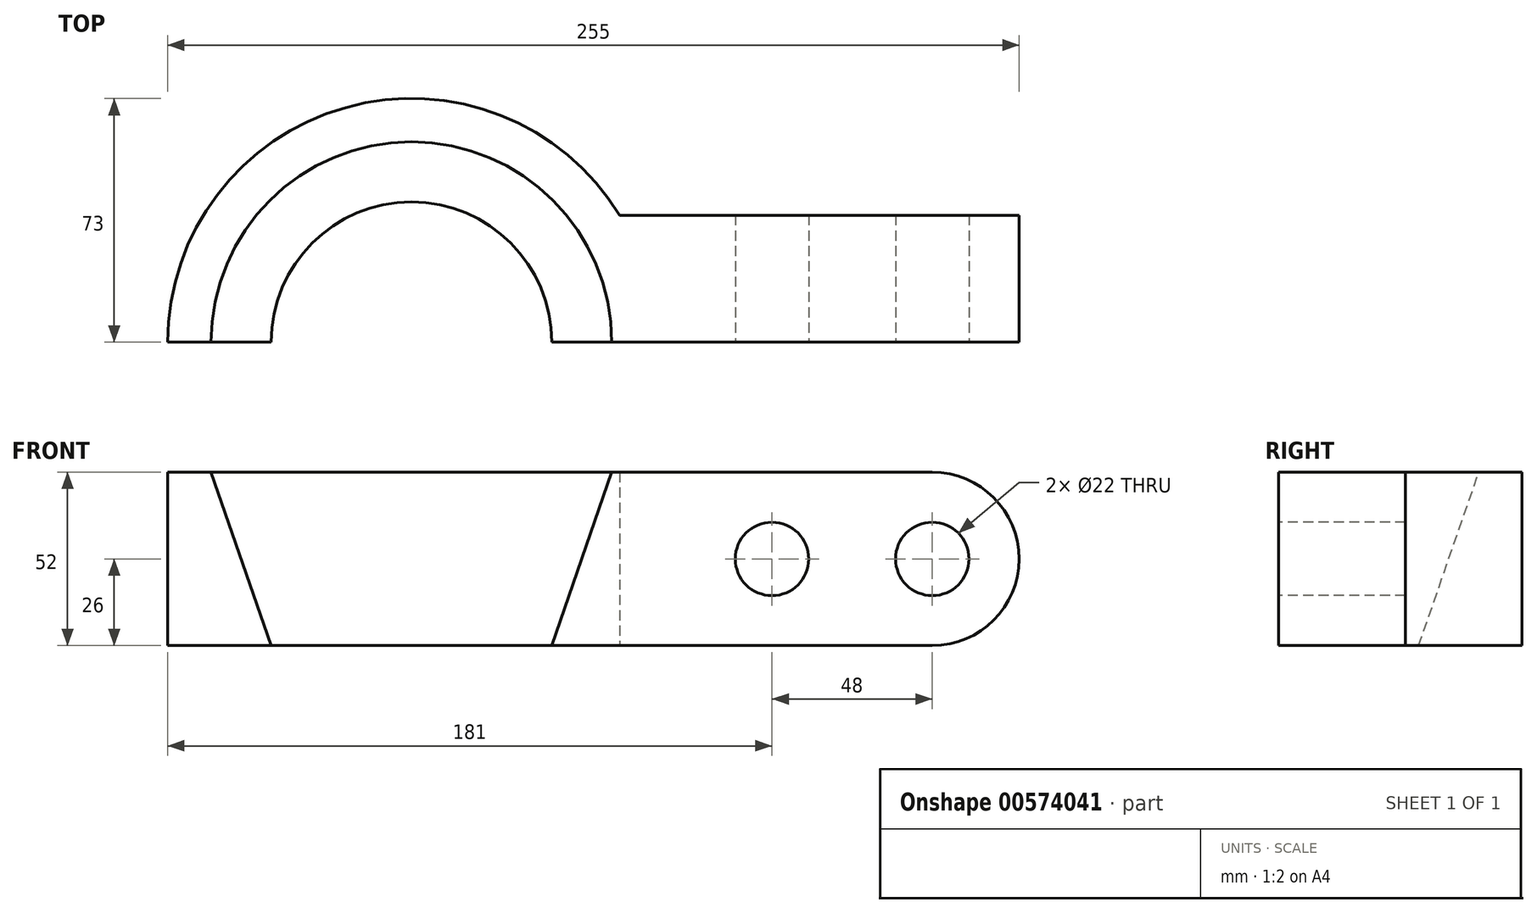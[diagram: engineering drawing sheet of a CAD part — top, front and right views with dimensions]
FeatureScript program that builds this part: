
annotation { "Feature Type Name" : "Feature", "Feature Type Description" : "" }
export const myFeature = defineFeature(function(context is Context, id is Id, definition is map)
    precondition{}
    {
        {
            var Q0;
            Q0=qCreatedBy(makeId("Top.planeOp"),FACE);
            var sketch = newSketch(context, id + "F0", { "sketchPlane" : qUnion([Q0])});
            skArc(sketch, "E0", {"start": v(62.33, 38) * mm, "mid": v(-19.73, 70.28) * mm, "end": v(-73, 0) * mm});
            skArc(sketch, "E1", {"start": v(42, 0) * mm, "mid": v(0, 42) * mm, "end": v(-42, 0) * mm});
            skLineSegment(sketch, "E2.bottom", {"start": v(42, 0) * mm, "end": v(182, 0) * mm});
            skLineSegment(sketch, "E2.top", {"start": v(62.33, 38) * mm, "end": v(182, 38) * mm});
            skLineSegment(sketch, "E2.right", {"start": v(182, 0) * mm, "end": v(182, 38) * mm});
            skLineSegment(sketch, "E3", {"start": v(42, 0) * mm, "end": v(-73, 0) * mm, "construction": true});
            skLineSegment(sketch, "E4", {"start": v(-42, 0) * mm, "end": v(-73, 0) * mm});
            skSolve(sketch);
        }
        {
            var Q0;
            Q0=makeQuery(id+"F0.imprint","IMPRINT",FACE,{"disambiguationData":[TD([[makeQuery(id+"F0.imprint","IMPRINT",EDGE,{"derivedFrom":sQuery(id+"F0.wireOp",EDGE,"E0")}),1.0]])]});
            extrude(context, id + "F1", {"entities" : qUnion([Q0]), "depth" : 52 * mm, "offsetDistance" : 25 * mm});
        }
        {
            var Q0;
            Q0=qCreatedBy(makeId("Front.planeOp"),FACE);
            var sketch = newSketch(context, id + "F2", { "sketchPlane" : qUnion([Q0])});
            skLineSegment(sketch, "E5", {"start": v(0, 0) * mm, "end": v(0, 52) * mm});
            skLineSegment(sketch, "E6", {"start": v(0, 52) * mm, "end": v(-60, 52) * mm});
            skLineSegment(sketch, "E7", {"start": v(-60, 52) * mm, "end": v(-42, 0) * mm});
            skLineSegment(sketch, "E8", {"start": v(-42, 0) * mm, "end": v(0, 0) * mm});
            skSolve(sketch);
        }
        {
            var Q0;
            Q0=makeQuery(id+"F2.imprint","IMPRINT",FACE,{"disambiguationData":[TD([[makeQuery(id+"F2.imprint","IMPRINT",EDGE,{"derivedFrom":sQuery(id+"F2.wireOp",EDGE,"E5")}),1.0]])]});
            var Q1;
            Q1=sQuery(id+"F2.wireOp",EDGE,"E5");
            revolve(context, id + "F3", {"operationType" : NewBodyOperationType.REMOVE, "entities" : qUnion([Q0]), "axis" : qUnion([Q1]), "revolveType" : RevolveType.FULL, "oppositeDirection" : true});
        }
        {
            var Q0;
            Q0=makeQuery(id+"F1.opExtrude","SWEPT_FACE",FACE,{"disambiguationData":[OSD([sQuery(id+"F0.wireOp",EDGE,"E2.bottom")])]});
            var sketch = newSketch(context, id + "F4", { "sketchPlane" : qUnion([Q0])});
            skCircle(sketch, "E9", {"center": v(108, 26) * mm, "radius": 11 * mm});
            skCircle(sketch, "E10", {"center": v(156, 26) * mm, "radius": 11 * mm});
            skSolve(sketch);
        }
        {
            var Q0;
            Q0=makeQuery(id+"F4.imprint","IMPRINT",FACE,{"disambiguationData":[TD([[makeQuery(id+"F4.imprint","IMPRINT",EDGE,{"derivedFrom":sQuery(id+"F4.wireOp",EDGE,"E9")}),1.0]])]});
            var Q1;
            Q1=makeQuery(id+"F4.imprint","IMPRINT",FACE,{"disambiguationData":[TD([[makeQuery(id+"F4.imprint","IMPRINT",EDGE,{"derivedFrom":sQuery(id+"F4.wireOp",EDGE,"E10")}),1.0]])]});
            extrude(context, id + "F5", {"entities" : qUnion([Q0, Q1]), "operationType" : NewBodyOperationType.REMOVE, "oppositeDirection" : true, "depth" : 57 * mm, "offsetDistance" : 25 * mm});
        }
        {
            var Q0;
            Q0=makeQuery(id+"F1.opExtrude","CAP_EDGE",EDGE,{"disambiguationData":[OSD([sQuery(id+"F0.wireOp",EDGE,"E2.right")])],"isStart":false});
            var Q1;
            Q1=makeQuery(id+"F1.opExtrude","CAP_EDGE",EDGE,{"disambiguationData":[OSD([sQuery(id+"F0.wireOp",EDGE,"E2.right")])],"isStart":true});
            fillet(context, id + "F6", {"entities" : qUnion([Q0, Q1]), "radius" : 26 * mm, "tangentPropagation" : true, "allowEdgeOverflow" : false});
        }
    });
